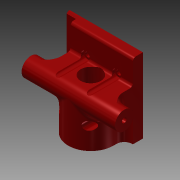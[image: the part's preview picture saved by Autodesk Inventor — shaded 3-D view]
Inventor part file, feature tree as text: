
AUTODESK INVENTOR PART (.ipt)
format: ipt  version: 2015 SP1 (Build 190203100, 203)  size: 318,976 bytes
history: native  units: in
note: dims shown in document units (in); Inventor stores cm internally (conversion verified against a paired STEP export)
features: reference x12, sketch x9, extrude x7, hole x2, plane x1, fillet x1
ambient origin geometry x8: Origin, YZ Plane, XZ Plane, XY Plane, X Axis, Y Axis, Z Axis, Center Point
bodies: Solid1 (feature_tree)
feature tree (32):
  extrude  "Extrusion1"  Depth=1.1811in TaperAngle=0.0deg
  extrude  "Extrusion5"  Depth=0.7874in TaperAngle=0.0deg
  extrude  "Extrusion6"  Depth=0.0394in
  extrude  "Extrusion2"  Depth=0.0394in
  extrude  "Extrusion8"  Depth=0.2756in TaperAngle=0.0deg
  extrude  "Extrusion3"  Depth=0.4331in
  extrude  "Extrusion7"  Depth=0.0787in
  plane  "Work Plane1"
  hole  "Hole1"  [1 undecoded]
  hole  "Hole2"  [1 undecoded]
  fillet  "Fillet2"  Radius=0.2756in
  sketch  "Sketch1"  dims[d0=1.5748in d1=1.1811in d2=0.0in]
  reference  "Reference1"
  reference  "Reference2"
  reference  "Reference3"
  reference  "Reference4"
  sketch  "Sketch2"  dims[d3=0.1181in d5=0.7874in d6=0.0in]
  sketch  "Sketch3"  dims[d7=0.0787in d8=0.0394in]
  sketch  "Sketch5"  dims[d9=0.0394in d10=0.0394in]
  sketch  "Sketch6"  dims[d11=0.0394in d12=0.2756in d13=0.0in]
  reference  "Reference6"
  sketch  "Sketch7"  dims[d14=0.0787in d15=0.4331in]
  sketch  "Sketch8"  dims[d19=0.0787in d20=0.0787in]
  reference  "Reference11"
  reference  "Reference12"
  reference  "Reference13"
  reference  "Reference14"
  sketch  "Sketch9"  dims[d21=0.2756in d22=0.0in d23=0.5118in]
  reference  "Reference15"
  reference  "Reference16"
  reference  "Reference17"
  sketch  "Sketch10"  dims[d24=0.5295in d25=0.2756in d26=0.0in d27=0.2756in d28=0.0in d30=0.122in d31=0.2362in d32=0.2165in d33=0.9055in d34=90.0deg d35=0.315in d36=0.8108in d37=0.2362in d38=0.0968in d39=0.2362in d40=0.2559in d41=0.1181in d42=90.0deg d43=0.3465in d44=0.8108in d46=2.3622in d47=0.0in d48=0.1969in]
note: 2 required parameter values undecoded (feature->parameter linkage not recoverable at this tier; creation-order binding heuristic only, values carry confidence <= 0.55)
